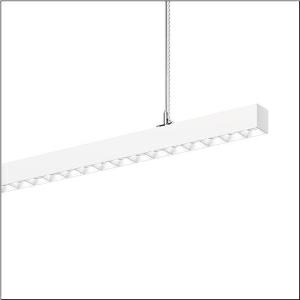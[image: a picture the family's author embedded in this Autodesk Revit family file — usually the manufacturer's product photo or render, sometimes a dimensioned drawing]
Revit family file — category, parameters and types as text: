
# Revit family: silica_r__21_51mx36dc4dwb_53ae
name_source: partatom
category: Lighting Fixtures
units: mm (PartAtom-declared; Revit-internal decimal feet)

## family parameters
Cut with Voids When Loaded = No
Host = Face
Light Source = No
Part Type = Normal
Room Calculation Point = No
Round Connector Dimension = Use Diameter
Shared = No

## types (1)
- --- (1 x LED, 17650 lm, 97.4 W, 4000K)
    Apparent Load = 97 VA
    CIE Flux Codes = 83 98 100 61 100
    Color Rendering = 80
    Color Temperature = 4000K
    Default Elevation = 1800 mm
    Description = Silica® 21, office luminaire, primary light control with darklight reflector, of PMMA, white, CAT 2 (L<= 3000cd/m²), light emission: direct/indirect distribution, primary light characteristic: symmetric, installation type: suspended mounting, LED, rated luminous flux: 17.650lm, luminous efficacy: 181lm/W, light colour: 840, colour temperature: 4000K, with terminal, 3+2-pole, max. 2.5mm², mains connection: 220..240V, AC, 50/60Hz, rated input power: 97.4W, luminaire housing, of aluminium, traffic white (RAL 9016), length: 3.004mm, width: 53mm, height: 53mm, protection rating (complete): IP20, insulation class (complete): insulation class I (protective earthing), certification: CE, permissible operating ambient temperature: 0..+35°C, standard: EN 50419, packaging unit: 1 piece
    Height = 53 mm
    Lamp = 1 x LED
    Lamp Light Flux = 17650 lm
    Lamp Power = 97.4 W
    Lamp count = 1
    Length = 3004 mm
    Luminous efficacy = 181 lm/W
    Manufacturer = Siteco
    ModVariant = No
    Model = 51MX36DC4DWB
    Mounting Place = Ceiling
    Mounting Type = Pendant
    Number of Poles = 1
    OnlyDefault = Yes
    Power Factor = 1
    Product Name = Silica® 21
    Product group = office luminaire | ceiling pendant
    ProductGroupID = 902
    Protection Class = Protection class I
    Protection Degree = IP 20
    RLX_Detail_Level = 1
    RLX_Emergency_Light_Flux = 0 lm
    RLX_Emergency_Type = 0
    RLX_Emergency_Type_DB = No
    RlxData = <blob elided: 62485 chars, md5=6201a078>
    Socket = socket
    Standby Power = 0 W
    System Light Flux = 17650 lm
    System Power = 97 W
    Type Comments = factory setting: luminous flux: 100 % | dim-lin: 254 | 336 mA
    Type Image = l_1335921.jpg
    URL = http://relux.com
    VarID = @adj_090983
    Voltage = 0 V
    Weight = 0.00 kg
    Width = 53 mm

## geometry (parser evidence)
native form markers: Blend x4, Sweep x12
no freeform markers — native parametric forms only
